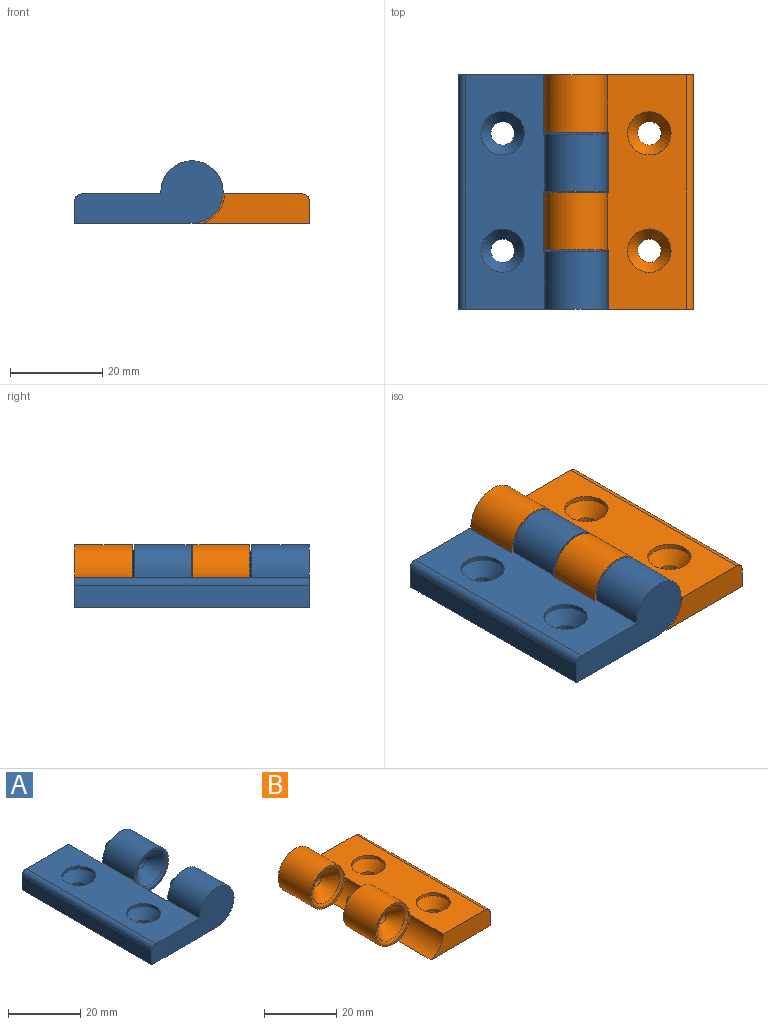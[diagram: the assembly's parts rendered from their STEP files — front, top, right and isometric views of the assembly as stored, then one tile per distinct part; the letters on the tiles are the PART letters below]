
ASSEMBLY  parts=2 mates=1
PART A: 28 faces, bbox 33.7x50.8x16.7 mm
  f0: cylinder r=6.75mm len=13.49mm, axis (0,-1,0), area 396mm2, adj f2,f3,f15,f18
  f1: plane 23.05x6.35mm, normal (0,1,0), area 124.1mm2, adj f2,f3,f4,f13,f17
  f2: plane 50.8x25.4mm, normal (0,0,-1), area 1188.7mm2, adj f0,f1,f4,f5,f6,f9,f12,f14
  f3: plane 50.8x17.08mm, normal (0,0,1), area 718.5mm2, adj f0,f1,f5,f6,f7,f10,f13,f14
  f4: plane 50.8x4.76mm, normal (-1,0,0), area 241.9mm2, adj f1,f2,f6,f13
  f5: cylinder r=6.75mm len=13.49mm, axis (0,-1,0), area 402.4mm2, adj f2,f3,f6,f16
  f6: plane 32.15x13.49mm, normal (0,-1,0), area 270.7mm2, adj f2,f3,f4,f5,f13
  f7: cylinder r=4.7mm len=9.4mm, axis (0,0,1), area 30mm2, adj f3,f8
  f8: cone r=4.7mm half-angle=35deg, axis (0,0,1), area 85.6mm2, adj f7,f9
  f9: cylinder r=2.54mm len=5.08mm, axis (0,0,1), area 35.9mm2, adj f2,f8
  f10: cylinder r=4.7mm len=9.4mm, axis (0,0,1), area 30mm2, adj f3,f11
  f11: cone r=4.7mm half-angle=35deg, axis (0,0,1), area 85.6mm2, adj f10,f12
  f12: cylinder r=2.54mm len=5.08mm, axis (0,0,1), area 35.9mm2, adj f2,f11
  f13: cylinder r=1.59mm len=50.8mm, axis (0,-1,0), area 126.7mm2, adj f1,f3,f4,f6
  f14: cylinder r=7.14mm len=13.1mm, axis (0,-1,0), area 110.4mm2, adj f2,f3,f15,f16
  f15: plane 13.88x13.49mm, normal (0,-1,0), area 19.9mm2, adj f0,f2,f3,f14,f27
  f16: plane 13.88x13.49mm, normal (0,1,0), area 19.9mm2, adj f2,f3,f5,f14,f20
  f17: cylinder r=7.14mm len=12.9mm, axis (0,1,0), area 108.8mm2, adj f1,f2,f3,f18
  f18: plane 13.88x13.49mm, normal (0,1,0), area 19.9mm2, adj f0,f2,f3,f17,f23
  f19: cone r=4.99mm half-angle=45deg, axis (0,-1,0), area 102.7mm2, adj f20,f21
  f20: torus R=6.35mm, axis (0,-1,0), area 53.3mm2, adj f16,f19
  f21: sphere r=1.92mm, area 6.8mm2, adj f19
  f22: cone r=4.99mm half-angle=45deg, axis (0,-1,0), area 102.7mm2, adj f23,f24
  f23: torus R=6.35mm, axis (0,-1,0), area 53.3mm2, adj f18,f22
  f24: sphere r=1.92mm, area 6.8mm2, adj f22
  f25: sphere r=2.31mm, area 9.8mm2, adj f26
  f26: cone r=5.28mm half-angle=45deg, axis (0,-1,0), area 111.8mm2, adj f25,f27
  f27: torus R=6.35mm, axis (0,1,0), area 43.4mm2, adj f15,f26
PART B: 28 faces, bbox 33.7x50.8x16.7 mm
  f0: cylinder r=6.75mm len=13.49mm, axis (0,-1,0), area 396mm2, adj f1,f2,f15,f17
  f1: plane 50.8x17.08mm, normal (0,0,1), area 718.5mm2, adj f0,f3,f5,f6,f7,f10,f13,f14
  f2: plane 50.8x25.4mm, normal (0,0,-1), area 1188.7mm2, adj f0,f3,f4,f5,f6,f9,f12,f14
  f3: cylinder r=6.75mm len=13.49mm, axis (0,-1,0), area 402.4mm2, adj f1,f2,f5,f16
  f4: plane 50.8x4.76mm, normal (1,0,0), area 241.9mm2, adj f2,f5,f6,f13
  f5: plane 32.15x13.49mm, normal (0,1,0), area 270.7mm2, adj f1,f2,f3,f4,f13
  f6: plane 23.05x6.35mm, normal (0,-1,0), area 124.1mm2, adj f1,f2,f4,f13,f18
  f7: cylinder r=4.7mm len=9.4mm, axis (0,0,-1), area 30mm2, adj f1,f8
  f8: cone r=4.7mm half-angle=35deg, axis (0,0,1), area 85.6mm2, adj f7,f9
  f9: cylinder r=2.54mm len=5.08mm, axis (0,0,-1), area 35.9mm2, adj f2,f8
  f10: cylinder r=4.7mm len=9.4mm, axis (0,0,-1), area 30mm2, adj f1,f11
  f11: cone r=4.7mm half-angle=35deg, axis (0,0,1), area 85.6mm2, adj f10,f12
  f12: cylinder r=2.54mm len=5.08mm, axis (0,0,-1), area 35.9mm2, adj f2,f11
  f13: cylinder r=1.59mm len=50.8mm, axis (0,1,0), area 126.7mm2, adj f1,f4,f5,f6
  f14: cylinder r=7.14mm len=13.1mm, axis (0,1,0), area 110.4mm2, adj f1,f2,f15,f16
  f15: plane 13.88x13.49mm, normal (0,1,0), area 19.9mm2, adj f0,f1,f2,f14,f26
  f16: plane 13.88x13.49mm, normal (0,-1,0), area 19.9mm2, adj f1,f2,f3,f14,f24
  f17: plane 13.88x13.49mm, normal (0,-1,0), area 19.9mm2, adj f0,f1,f2,f18,f21
  f18: cylinder r=7.14mm len=12.9mm, axis (0,-1,0), area 108.8mm2, adj f1,f2,f6,f17
  f19: sphere r=2.31mm, area 9.8mm2, adj f20
  f20: cone r=5.28mm half-angle=45deg, axis (0,-1,0), area 111.8mm2, adj f19,f21
  f21: torus R=6.35mm, axis (0,1,0), area 43.4mm2, adj f17,f20
  f22: sphere r=2.31mm, area 9.8mm2, adj f23
  f23: cone r=5.28mm half-angle=45deg, axis (0,-1,0), area 111.8mm2, adj f22,f24
  f24: torus R=6.35mm, axis (0,1,0), area 43.4mm2, adj f16,f23
  f25: cone r=4.99mm half-angle=45deg, axis (0,-1,0), area 102.7mm2, adj f26,f27
  f26: torus R=6.35mm, axis (0,-1,0), area 53.3mm2, adj f15,f25
  f27: sphere r=1.92mm, area 6.8mm2, adj f25
PLACE A t=(13.18,-25.08,0)mm
PLACE B rot(axis=(0,1,0),0deg) t=(13.18,-25.08,0)mm
MATE revolute A.f0 <-> B.f0  axis (0,1,0) through (13.18,-12.58,6.75)mm
